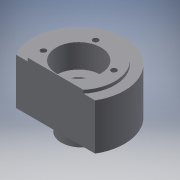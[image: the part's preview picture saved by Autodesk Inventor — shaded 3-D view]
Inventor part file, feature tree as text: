
AUTODESK INVENTOR PART (.ipt)
format: ipt  version: 2016 (Build 200138000, 138)  size: 146,432 bytes
history: native  units: mm
features: sketch x7, extrude x6, reference x3, hole x1
ambient origin geometry x8: Origin, YZ Plane, XZ Plane, XY Plane, X Axis, Y Axis, Z Axis, Center Point
bodies: Solid1 (feature_tree)
feature tree (17):
  extrude  "Extrusion1"  Depth=35.0mm TaperAngle=0.0deg
  extrude  "Extrusion2"  Depth=2.5mm TaperAngle=0.0deg
  extrude  "Extrusion3"  Depth=18.0mm TaperAngle=0.0deg
  extrude  "Extrusion4"  Depth=18.0mm TaperAngle=0.0deg
  extrude  "Extrusion5"  Depth=3.3mm
  extrude  "Extrusion6"  Depth=10.0mm TaperAngle=0.0deg
  hole  "Hole1"  [1 undecoded]
  sketch  "Sketch1"  dims[d0=69.5mm d1=35.0mm d2=0.0mm]
  sketch  "Sketch2"  dims[d3=55.0mm d4=2.5mm d5=0.0mm]
  sketch  "Sketch3"  dims[d6=34.0mm d7=18.0mm d8=0.0mm]
  sketch  "Sketch4"  dims[d9=19.7mm d10=18.0mm d11=0.0mm]
  sketch  "Sketch5"  dims[d12=30.0mm d13=3.3mm]
  sketch  "Sketch6"  dims[d14=7.0mm d15=10.0mm d16=0.0mm]
  sketch  "Sketch7"  dims[d17=52.3mm d18=10.0mm d19=0.0mm d20=4.134mm d21=10.0mm d22=4.0mm d23=2.0mm d24=90.0deg d25=14.2mm d26=20.594885mm]
  reference  "Reference1"
  reference  "Reference2"
  reference  "Reference3"
note: 1 required parameter value undecoded (feature->parameter linkage not recoverable at this tier; creation-order binding heuristic only, values carry confidence <= 0.55)
